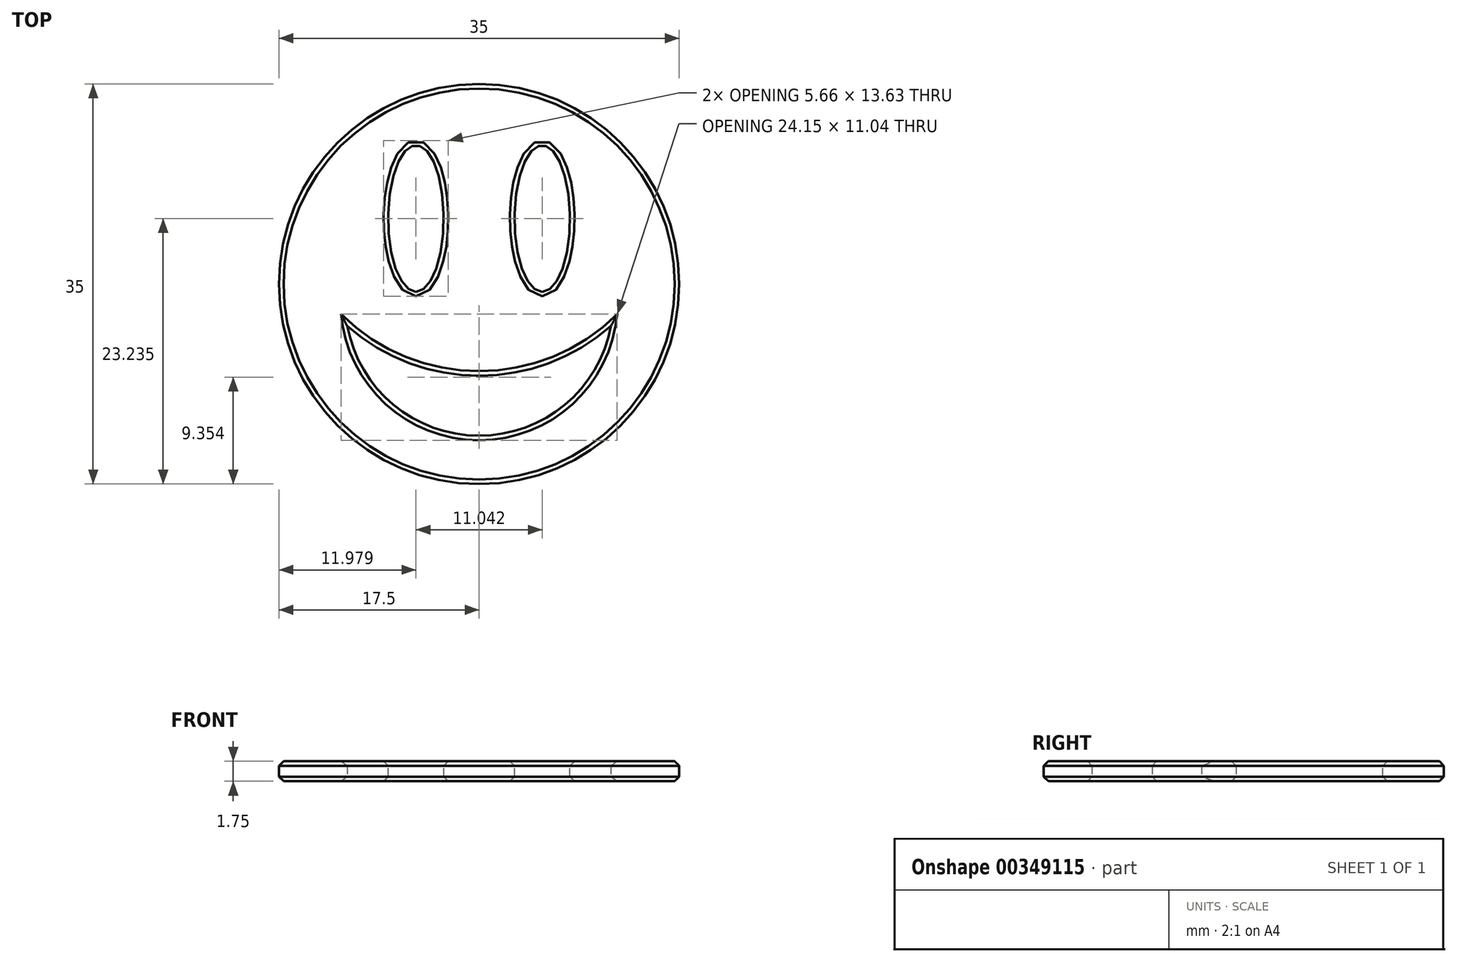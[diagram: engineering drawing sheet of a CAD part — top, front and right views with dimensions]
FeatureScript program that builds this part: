
annotation { "Feature Type Name" : "Feature", "Feature Type Description" : "" }
export const myFeature = defineFeature(function(context is Context, id is Id, definition is map)
    precondition{}
    {
        {
            var Q0;
            Q0=qCreatedBy(makeId("Top.planeOp"),FACE);
            var sketch = newSketch(context, id + "F0", { "sketchPlane" : qUnion([Q0])});
            skCircle(sketch, "E0", {"center": v(0, 0) * mm, "radius": 17.5 * mm});
            skEllipse(sketch, "E1", {"center": v(-5.52, 5.73) * mm, "majorRadius": 6.42 * mm, "minorRadius": 2.43 * mm, "majorAxis": v(0, -1)});
            skLineSegment(sketch, "E2", {"start": v(0, 17.5) * mm, "end": v(0, -17.5) * mm, "construction": true});
            skArc(sketch, "E3", {"start": v(-11.53, -3.68) * mm, "mid": v(-7.5, -10.56) * mm, "end": v(0, -13.27) * mm});
            skArc(sketch, "E4", {"start": v(-11.53, -3.68) * mm, "mid": v(-6.16, -6.9) * mm, "end": v(0, -8.02) * mm});
            skArc(sketch, "E5.MirrorCS", {"start": v(11.53, -3.68) * mm, "mid": v(7.5, -10.56) * mm, "end": v(0, -13.27) * mm});
            skArc(sketch, "E6.MirrorCS", {"start": v(11.53, -3.68) * mm, "mid": v(6.16, -6.9) * mm, "end": v(0, -8.02) * mm});
            skEllipse(sketch, "E7.MirrorC", {"center": v(5.52, 5.73) * mm, "majorRadius": 6.42 * mm, "minorRadius": 2.43 * mm, "majorAxis": v(0, -1)});
            skSolve(sketch);
        }
        {
            var Q0;
            Q0 = qSketchRegion(id + "F0", true);
            extrude(context, id + "F1", {"entities" : qUnion([Q0]), "depth" : 1.75 * mm});
        }
        {
            var Q0;
            Q0=makeQuery(id+"F1.opExtrude","CAP_FACE",FACE,{"disambiguationData":[OSD([sQuery(id+"F0.wireOp",EDGE,"E0"),sQuery(id+"F0.wireOp",EDGE,"E1"),sQuery(id+"F0.wireOp",EDGE,"E3"),sQuery(id+"F0.wireOp",EDGE,"E4"),sQuery(id+"F0.wireOp",EDGE,"E5.MirrorCS"),sQuery(id+"F0.wireOp",EDGE,"E6.MirrorCS"),sQuery(id+"F0.wireOp",EDGE,"E7.MirrorC")])],"isStart":false});
            var Q1;
            Q1=makeQuery(id+"F1.opExtrude","CAP_FACE",FACE,{"disambiguationData":[OSD([sQuery(id+"F0.wireOp",EDGE,"E0"),sQuery(id+"F0.wireOp",EDGE,"E1"),sQuery(id+"F0.wireOp",EDGE,"E3"),sQuery(id+"F0.wireOp",EDGE,"E4"),sQuery(id+"F0.wireOp",EDGE,"E5.MirrorCS"),sQuery(id+"F0.wireOp",EDGE,"E6.MirrorCS"),sQuery(id+"F0.wireOp",EDGE,"E7.MirrorC")])],"isStart":true});
            chamfer(context, id + "F2", {"entities" : qUnion([Q0, Q1]), "width" : .4 * mm, "tangentPropagation" : true});
        }
    });
